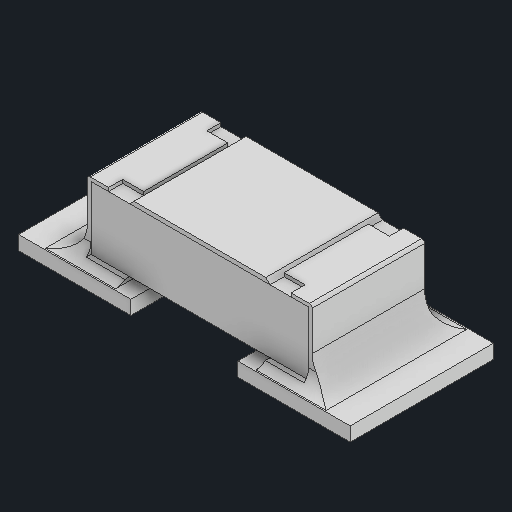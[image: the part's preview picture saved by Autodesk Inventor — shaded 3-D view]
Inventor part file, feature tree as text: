
AUTODESK INVENTOR PART (.ipt)
format: ipt  version: 2023 (Build 270158000, 158)  size: 139,264 bytes
history: native  units: in
note: dims shown in document units (in); Inventor stores cm internally (conversion verified against a paired STEP export)
features: other x2, fillet x2
ambient origin geometry x8: Origin, YZ Plane, XZ Plane, XY Plane, X Axis, Y Axis, Z Axis, Center Point
bodies: Solid1 (feature_tree), Solid2 (feature_tree), Solid3 (feature_tree), Solid4 (feature_tree)
feature tree (4):
  other  "Boss-Extrude1"
  other  "Boss-Extrude3"
  fillet  "Fillet6"  [1 undecoded]
  fillet  "Fillet5"  [1 undecoded]
note: 2 required parameter values undecoded (feature->parameter linkage not recoverable at this tier; creation-order binding heuristic only, values carry confidence <= 0.55)
